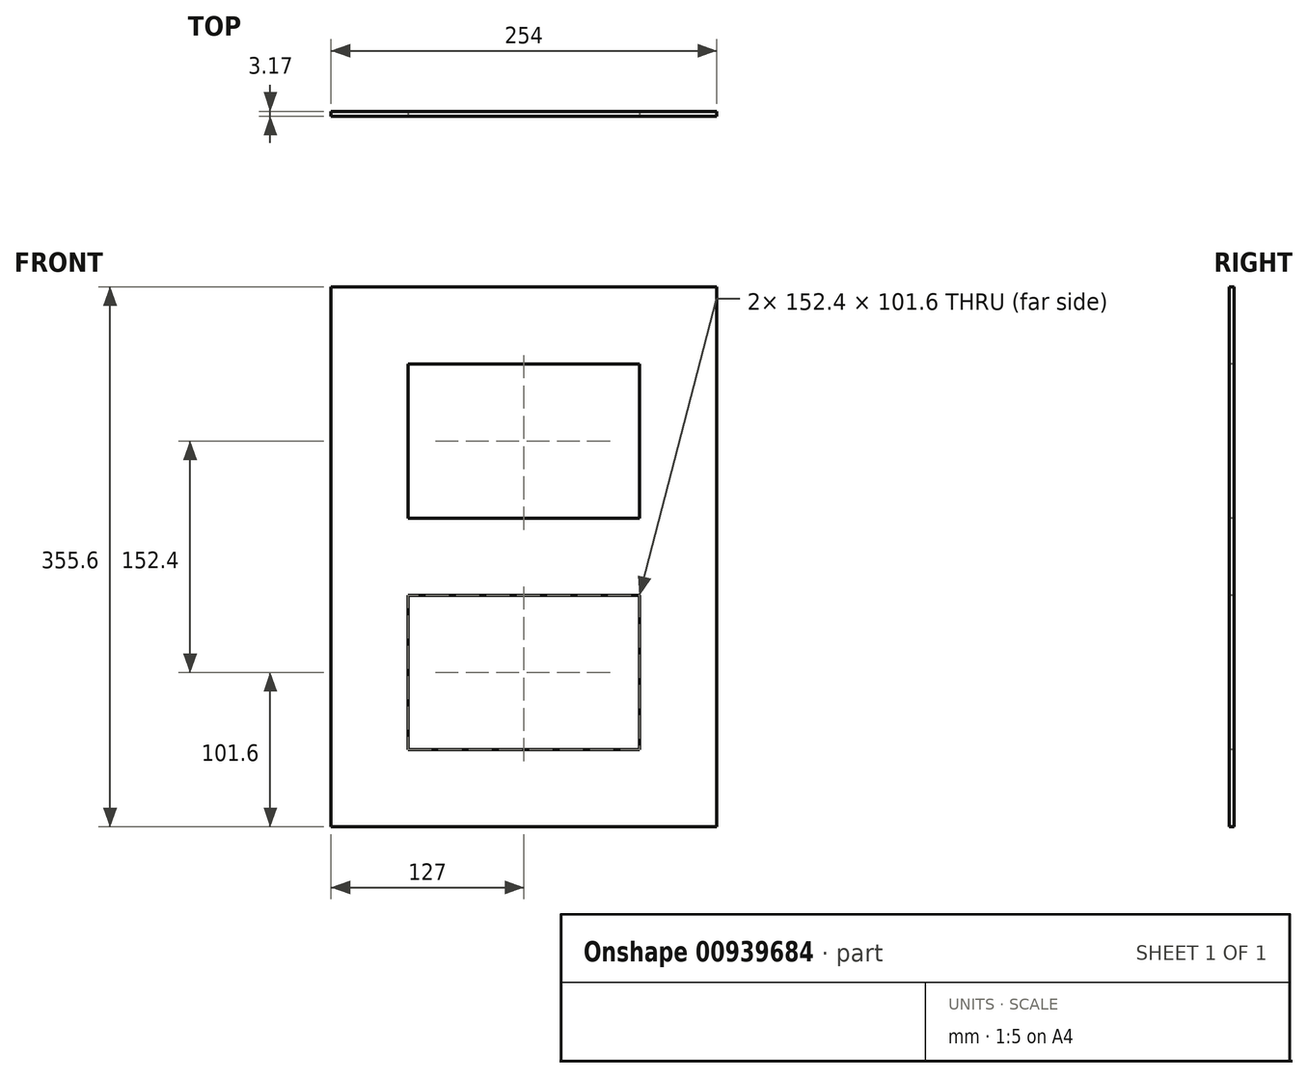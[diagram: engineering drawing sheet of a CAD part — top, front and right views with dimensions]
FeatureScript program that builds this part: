
annotation { "Feature Type Name" : "Feature", "Feature Type Description" : "" }
export const myFeature = defineFeature(function(context is Context, id is Id, definition is map)
    precondition{}
    {
        {
            var Q0;
            Q0=qCreatedBy(makeId("Front.planeOp"),FACE);
            var sketch = newSketch(context, id + "F0", { "sketchPlane" : qUnion([Q0])});
            skLineSegment(sketch, "E0.bottom", {"start": v(0, 0) * mm, "end": v(-254, 0) * mm});
            skLineSegment(sketch, "E0.top", {"start": v(0, 355.6) * mm, "end": v(-254, 355.6) * mm});
            skLineSegment(sketch, "E0.left", {"start": v(0, 0) * mm, "end": v(0, 355.6) * mm});
            skLineSegment(sketch, "E0.right", {"start": v(-254, 0) * mm, "end": v(-254, 355.6) * mm});
            skLineSegment(sketch, "E1.bottom", {"start": v(-203.2, 304.8) * mm, "end": v(-50.8, 304.8) * mm});
            skLineSegment(sketch, "E1.top", {"start": v(-203.2, 203.2) * mm, "end": v(-50.8, 203.2) * mm});
            skLineSegment(sketch, "E1.left", {"start": v(-203.2, 304.8) * mm, "end": v(-203.2, 203.2) * mm});
            skLineSegment(sketch, "E1.right", {"start": v(-50.8, 304.8) * mm, "end": v(-50.8, 203.2) * mm});
            skLineSegment(sketch, "E2.bottom", {"start": v(-203.2, 152.4) * mm, "end": v(-50.8, 152.4) * mm});
            skLineSegment(sketch, "E2.top", {"start": v(-203.2, 50.8) * mm, "end": v(-50.8, 50.8) * mm});
            skLineSegment(sketch, "E2.left", {"start": v(-203.2, 152.4) * mm, "end": v(-203.2, 50.8) * mm});
            skLineSegment(sketch, "E2.right", {"start": v(-50.8, 152.4) * mm, "end": v(-50.8, 50.8) * mm});
            skSolve(sketch);
        }
        {
            var Q0;
            Q0 = qSketchRegion(id + "F0", true);
            extrude(context, id + "F1", {"entities" : qUnion([Q0]), "oppositeDirection" : true, "depth" : 3.17 * mm, "offsetDistance" : 25.4 * mm});
        }
    });
